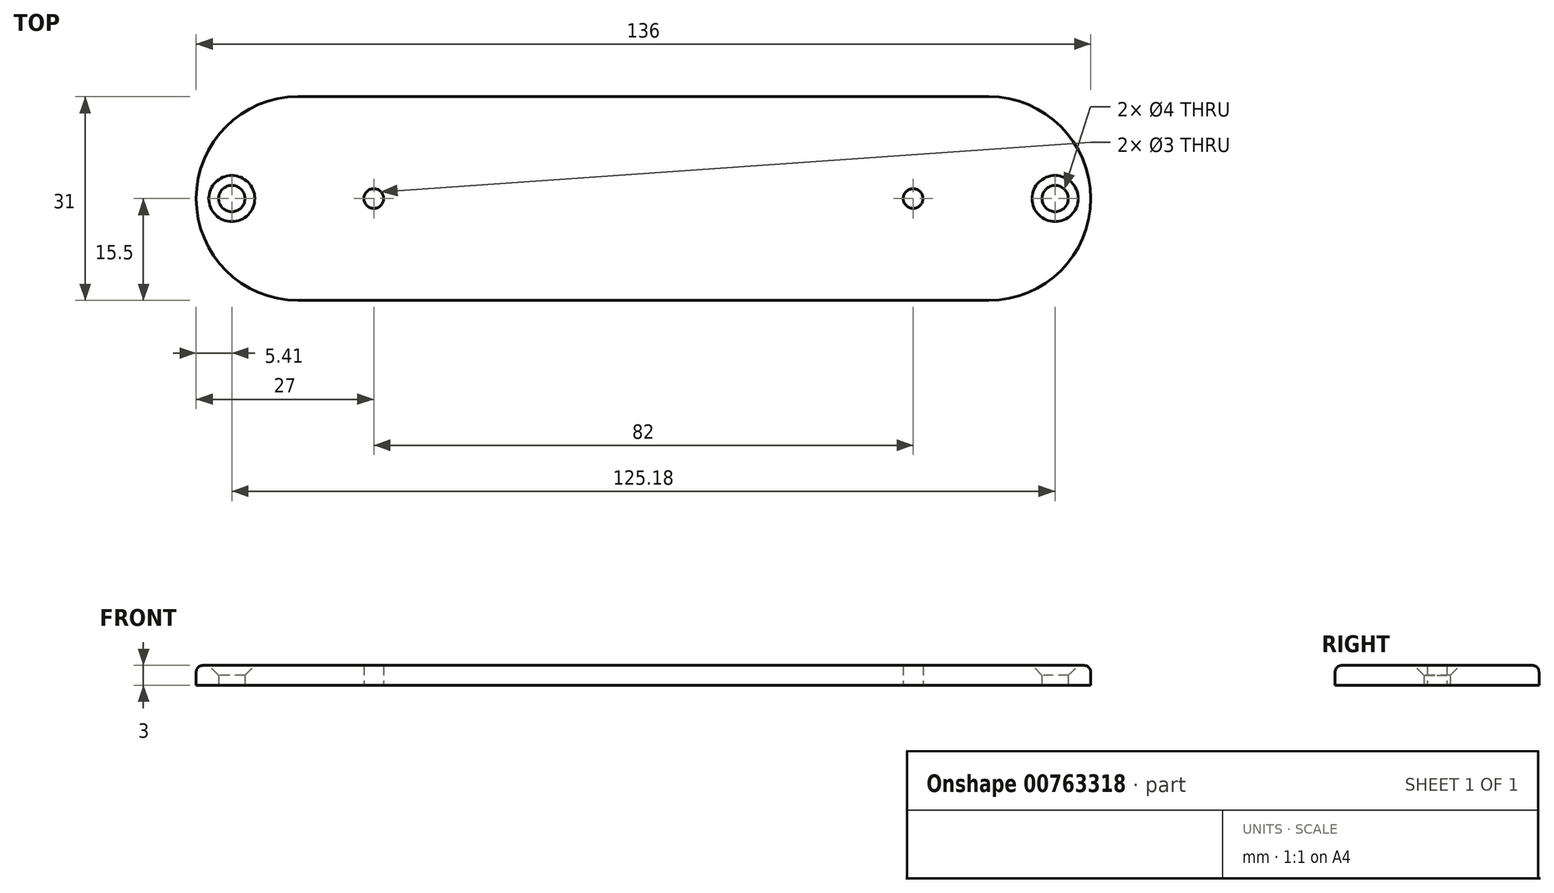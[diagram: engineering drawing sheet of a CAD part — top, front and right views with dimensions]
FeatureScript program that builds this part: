
annotation { "Feature Type Name" : "Feature", "Feature Type Description" : "" }
export const myFeature = defineFeature(function(context is Context, id is Id, definition is map)
    precondition{}
    {
        {
            var Q0;
            Q0=qCreatedBy(makeId("Top.planeOp"),FACE);
            var sketch = newSketch(context, id + "F0", { "sketchPlane" : qUnion([Q0])});
            skLineSegment(sketch, "E0.bottom", {"start": v(0, 0) * mm, "end": v(-105, 0) * mm});
            skLineSegment(sketch, "E0.top", {"start": v(0, 31) * mm, "end": v(-105, 31) * mm});
            skArc(sketch, "E1", {"start": v(0, 0) * mm, "mid": v(15.5, 15.5) * mm, "end": v(0, 31) * mm});
            skArc(sketch, "E2", {"start": v(-105, 31) * mm, "mid": v(-120.5, 15.5) * mm, "end": v(-105, 0) * mm});
            skLineSegment(sketch, "E3", {"start": v(-105, 31) * mm, "end": v(-105, 0) * mm, "construction": true});
            skLineSegment(sketch, "E4", {"start": v(0, 31) * mm, "end": v(0, 0) * mm, "construction": true});
            skCircle(sketch, "E5", {"center": v(-115.1, 15.5) * mm, "radius": 2 * mm});
            skCircle(sketch, "E6", {"center": v(-93.5, 15.5) * mm, "radius": 1.5 * mm});
            skCircle(sketch, "E7", {"center": v(10.09, 15.5) * mm, "radius": 2 * mm});
            skCircle(sketch, "E8", {"center": v(-11.5, 15.5) * mm, "radius": 1.5 * mm});
            skSolve(sketch);
        }
        {
            var Q0;
            Q0=makeQuery(id+"F0.imprint","IMPRINT",FACE,{"disambiguationData":[TD([[makeQuery(id+"F0.imprint","IMPRINT",EDGE,{"derivedFrom":sQuery(id+"F0.wireOp",EDGE,"E0.bottom")}),-1.0]])]});
            extrude(context, id + "F1", {"entities" : qUnion([Q0]), "depth" : 3 * mm, "offsetDistance" : 25 * mm});
        }
        {
            var Q0;
            Q0=makeQuery(id+"F1.opExtrude","CAP_EDGE",EDGE,{"disambiguationData":[OSD([sQuery(id+"F0.wireOp",EDGE,"E5")])],"isStart":false});
            var Q1;
            Q1=makeQuery(id+"F1.opExtrude","CAP_EDGE",EDGE,{"disambiguationData":[OSD([sQuery(id+"F0.wireOp",EDGE,"E7")])],"isStart":false});
            chamfer(context, id + "F2", {"entities" : qUnion([Q0, Q1]), "width" : 1.5 * mm, "tangentPropagation" : true});
        }
        {
            var Q0;
            Q0=makeQuery(id+"F1.opExtrude","CAP_EDGE",EDGE,{"disambiguationData":[OSD([sQuery(id+"F0.wireOp",EDGE,"E2")])],"isStart":false});
            var Q1;
            Q1=makeQuery(id+"F1.opExtrude","CAP_EDGE",EDGE,{"disambiguationData":[OSD([sQuery(id+"F0.wireOp",EDGE,"E0.bottom")])],"isStart":false});
            var Q2;
            Q2=makeQuery(id+"F1.opExtrude","CAP_EDGE",EDGE,{"disambiguationData":[OSD([sQuery(id+"F0.wireOp",EDGE,"E0.top")])],"isStart":false});
            var Q3;
            Q3=makeQuery(id+"F1.opExtrude","CAP_EDGE",EDGE,{"disambiguationData":[OSD([sQuery(id+"F0.wireOp",EDGE,"E1")])],"isStart":false});
            fillet(context, id + "F3", {"entities" : qUnion([Q0, Q1, Q2, Q3]), "radius" : 1 * mm, "tangentPropagation" : true, "allowEdgeOverflow" : false});
        }
    });
